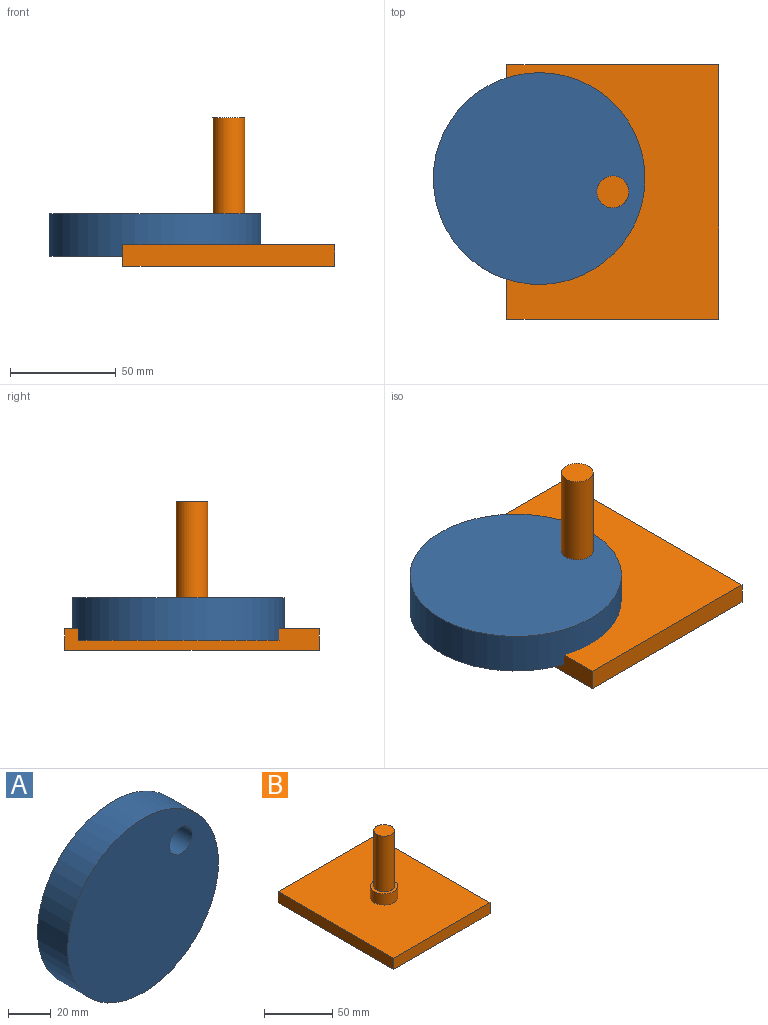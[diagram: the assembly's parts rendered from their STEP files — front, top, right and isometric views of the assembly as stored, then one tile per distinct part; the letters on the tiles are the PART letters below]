
ASSEMBLY  parts=2 mates=1
PART A: 4 faces, bbox 100x20x100 mm
  f0: plane 100x100mm, normal (0,-1,0), area 7677.3mm2, adj f2,f3
  f1: plane 100x100mm, normal (0,1,0), area 7677.3mm2, adj f2,f3
  f2: cylinder r=50mm len=100mm, axis (0,1,0), area 6283.2mm2, adj f0,f1
  f3: cylinder r=7.5mm len=20mm, axis (0,-1,0), area 942.5mm2, adj f0,f1
PART B: 10 faces, bbox 100x120x70 mm
  f0: plane 120x10mm, normal (1,0,0), area 1200mm2, adj f1,f3,f4,f5
  f1: plane 100x10mm, normal (0,1,0), area 1000mm2, adj f0,f2,f4,f5
  f2: plane 120x10mm, normal (-1,0,0), area 1200mm2, adj f1,f3,f4,f5
  f3: plane 100x10mm, normal (0,-1,0), area 1000mm2, adj f0,f2,f4,f5
  f4: plane 120x100mm, normal (0,0,1), area 11685.8mm2, adj f0,f1,f2,f3,f6
  f5: plane 120x100mm, normal (0,0,-1), area 12000mm2, adj f0,f1,f2,f3
  f6: cylinder r=10mm len=20mm, axis (0,0,-1), area 628.3mm2, adj f4,f7
  f7: plane 20x20mm, normal (0,0,1), area 137.4mm2, adj f6,f8
  f8: cylinder r=7.5mm len=50mm, axis (0,0,-1), area 2356.2mm2, adj f7,f9
  f9: plane 15x15mm, normal (0,0,1), area 176.7mm2, adj f8
PLACE A rot(axis=(0.91,0.29,0.29),95.1deg) t=(-209.08,-30.77,42.76)mm
PLACE B t=(-174.3,-37.09,27.98)mm fixed
MATE cylindrical A.f3 <-> B.f8  axis (0,0,1) through (-174.3,-37.09,52.76)mm
